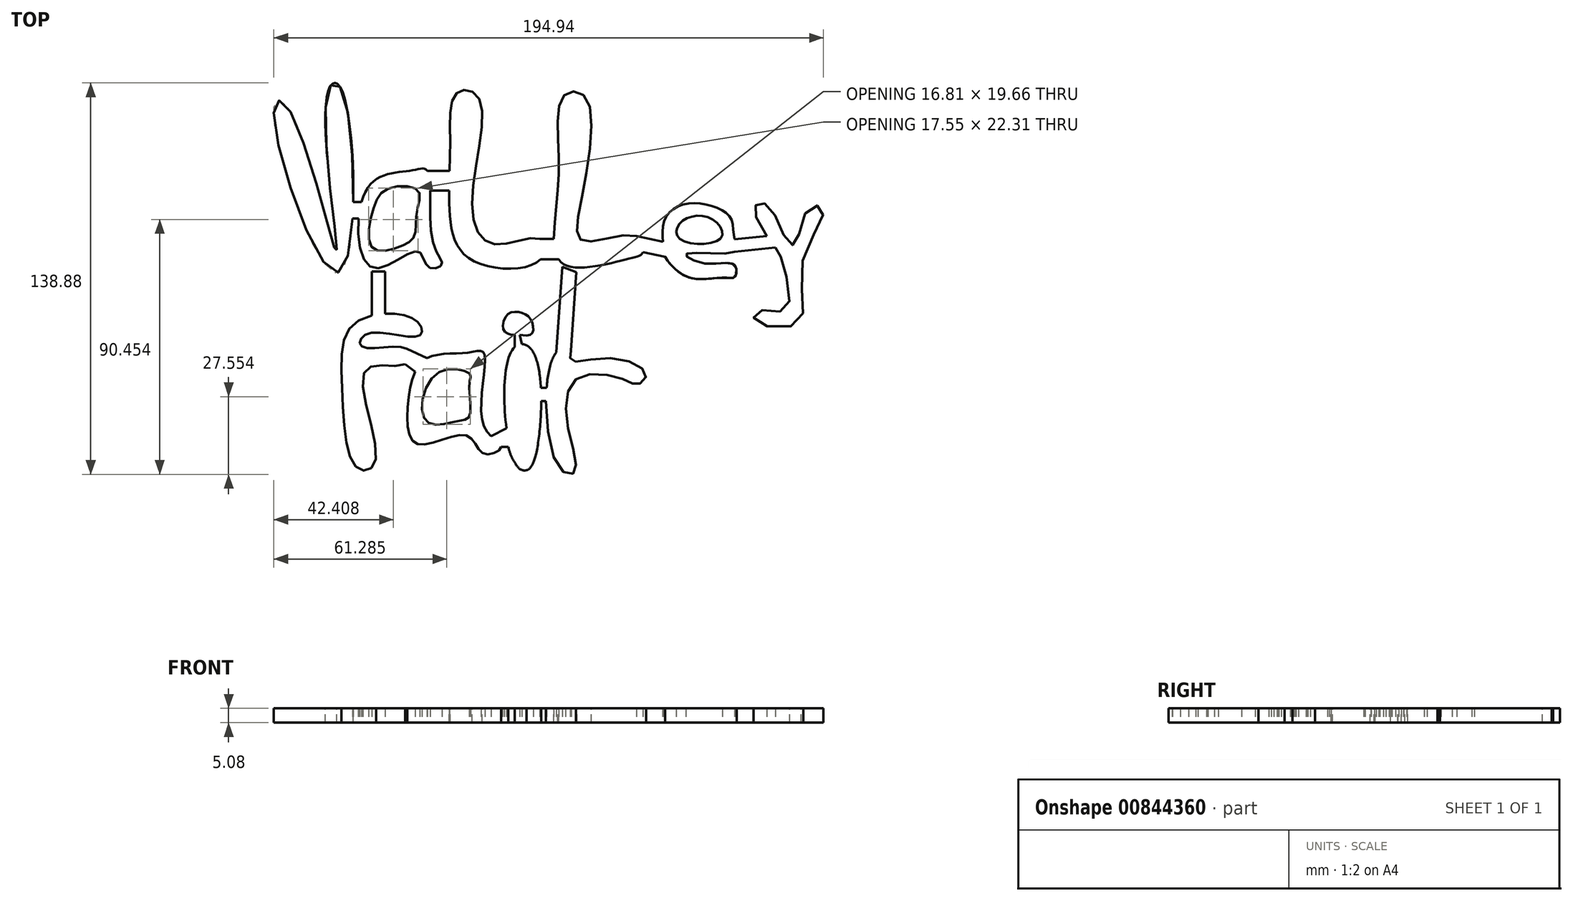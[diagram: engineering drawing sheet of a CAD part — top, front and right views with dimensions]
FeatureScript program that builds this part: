
annotation { "Feature Type Name" : "Feature", "Feature Type Description" : "" }
export const myFeature = defineFeature(function(context is Context, id is Id, definition is map)
    precondition{}
    {
        {
            var Q0;
            Q0=qCreatedBy(makeId("Top.planeOp"),FACE);
            var sketch = newSketch(context, id + "F0", { "sketchPlane" : qUnion([Q0])});
            skFitSpline(sketch, "E0", {"points": [v(-51.1, 46.73) * mm, v(-51.9, -19.2) * mm, v(-74.42, 39.6) * mm, v(-70.21, 40.25) * mm, v(-52.4, -11.9) * mm, v(-55.47, 44.78) * mm, v(-51.1, 46.73) * mm]});
            skFitSpline(sketch, "E1", {"points": [v(-25.67, 17.09) * mm, v(-41.38, 10.77) * mm, v(-39.6, -17.41) * mm, v(-23.57, -11.58) * mm, v(-19.84, -17.09) * mm, v(-15.14, -16.44) * mm, v(-18.06, -8.67) * mm, v(-20.16, 16.93) * mm, v(-25.67, 17.09) * mm]});
            skFitSpline(sketch, "E2", {"points": [v(-34.1, 10.6) * mm, v(-39.6, 2.51) * mm, v(-39.6, -10.45) * mm, v(-29.88, -9.96) * mm, v(-24.7, -6.07) * mm, v(-23.89, 2.19) * mm, v(-23.4, 9.96) * mm, v(-34.1, 10.6) * mm]});
            skFitSpline(sketch, "E3", {"points": [v(20, -14.5) * mm, v(-4.45, -14.66) * mm, v(-12.23, 2.19) * mm, v(-12.07, 26.8) * mm, v(-9.47, 44.78) * mm, v(-1.86, 42.68) * mm, v(-4.3, 5.1) * mm, v(3.8, -9.15) * mm, v(19.68, -7.2) * mm, v(20, -14.5) * mm]});
            skFitSpline(sketch, "E4", {"points": [v(52.07, -14) * mm, v(28.42, -16.28) * mm, v(25.19, 0) * mm, v(26.48, 23.4) * mm, v(28.42, 43.81) * mm, v(36.2, 42.68) * mm, v(33.93, 3.8) * mm, v(35.39, -8.02) * mm, v(54.01, -6.24) * mm, v(56.28, -11.9) * mm, v(52.07, -14) * mm]});
            skFitSpline(sketch, "E5", {"points": [v(69.4, -7.2) * mm, v(83.98, -6.88) * mm, v(80.58, 0) * mm, v(69.89, -1.21) * mm, v(69.4, -7.2) * mm]});
            skPoint(sketch, "E6.2.internal.orphan", {"position": v(87.54, 0) * mm});
            skFitSpline(sketch, "E7", {"points": [v(88.84, -7.37) * mm, v(87.54, 0) * mm, v(81.22, 4.3) * mm, v(70.86, 5.1) * mm, v(64.22, 0) * mm, v(63.4, -8.18) * mm, v(64.22, -13.52) * mm, v(70.37, -19.84) * mm, v(77.34, -21.46) * mm, v(86.08, -20.97) * mm, v(89, -20.65) * mm, v(88.84, -16.44) * mm, v(78.63, -15.95) * mm, v(71.67, -12.55) * mm, v(88.84, -11.74) * mm, v(88.84, -7.37) * mm]});
            skFitSpline(sketch, "E8", {"points": [v(103.26, -10.22) * mm, v(95.78, 2.45) * mm, v(97.22, 5.32) * mm, v(101.25, 4.17) * mm, v(107.87, -8.5) * mm, v(110.46, -8.78) * mm, v(115.35, 3.89) * mm, v(120.24, 3.02) * mm, v(112.76, -15.69) * mm, v(111.32, -36.98) * mm, v(96.07, -36.12) * mm, v(97.5, -32.67) * mm, v(107.3, -32.1) * mm, v(105.57, -14.53) * mm, v(103.26, -10.22) * mm]});
            skLineSegment(sketch, "E9", {"start": v(-46.4, 5.91) * mm, "end": v(-43.47, 5.91) * mm});
            skLineSegment(sketch, "E10", {"start": v(-46.64, 0) * mm, "end": v(-44.54, 0) * mm});
            skLineSegment(sketch, "E11", {"start": v(-20.16, 16.93) * mm, "end": v(-12.23, 16.93) * mm});
            skLineSegment(sketch, "E12", {"start": v(-12.23, 9.96) * mm, "end": v(-19.15, 9.96) * mm});
            skLineSegment(sketch, "E13", {"start": v(19.68, -7.2) * mm, "end": v(24.75, -7.2) * mm});
            skLineSegment(sketch, "E14", {"start": v(20, -14.5) * mm, "end": v(26.46, -14.5) * mm});
            skLineSegment(sketch, "E15", {"start": v(88.84, -11.74) * mm, "end": v(103.26, -10.22) * mm});
            skLineSegment(sketch, "E16", {"start": v(88.84, -7.37) * mm, "end": v(100.32, -6.16) * mm});
            skPoint(sketch, "E17.end.orphan", {"position": v(63.4, -11.9) * mm});
            skLineSegment(sketch, "E18", {"start": v(56.28, -11.9) * mm, "end": v(64.22, -13.52) * mm});
            skLineSegment(sketch, "E19", {"start": v(54.01, -6.24) * mm, "end": v(63.4, -8.18) * mm});
            skSolve(sketch);
        }
        {
            var Q0;
            Q0 = qSketchRegion(id + "F0", true);
            extrude(context, id + "F1", {"entities" : qUnion([Q0]), "depth" : 5.08 * mm, "offsetDistance" : 25.4 * mm});
        }
        {
            var Q0;
            Q0=qCreatedBy(makeId("Top.planeOp"),FACE);
            var sketch = newSketch(context, id + "F2", { "sketchPlane" : qUnion([Q0])});
            skFitSpline(sketch, "E20", {"points": [v(-5.2, -47.47) * mm, v(-20.26, -49.52) * mm, v(-26.76, -63.56) * mm, v(-23.68, -79.98) * mm, v(-6.23, -76.9) * mm, v(0, -83.4) * mm, v(6.1, -81.01) * mm, v(0, -73.82) * mm, v(0, -47.81) * mm, v(-5.2, -47.47) * mm]});
            skPoint(sketch, "E21.3.internal.orphan", {"position": v(-5.2, -70.06) * mm});
            skPoint(sketch, "E21.4.internal.orphan", {"position": v(-5.2, -55) * mm});
            skFitSpline(sketch, "E22", {"points": [v(-5.2, -55) * mm, v(-16.84, -55) * mm, v(-20.6, -71.77) * mm, v(-9.3, -71.77) * mm, v(-5.2, -70.06) * mm, v(-5.2, -58.42) * mm, v(-5.2, -55) * mm]});
            skFitSpline(sketch, "E23", {"points": [v(9.86, -46.79) * mm, v(10.88, -86.49) * mm, v(15, -89.23) * mm, v(18.41, -83.4) * mm, v(17.05, -46.79) * mm, v(9.86, -46.79) * mm]});
            skFitSpline(sketch, "E24", {"points": [v(33.47, -56.37) * mm, v(49.56, -57.05) * mm, v(54.7, -58.76) * mm, v(57.43, -55.34) * mm, v(45.11, -49.52) * mm, v(30.74, -50.2) * mm, v(30.74, -46.79) * mm, v(25.6, -47.47) * mm, v(26.29, -87.86) * mm, v(32.1, -89.91) * mm, v(29.37, -72.11) * mm, v(33.47, -56.37) * mm]});
            skPoint(sketch, "E25.6.internal.orphan", {"position": v(-27.45, -36.86) * mm});
            skPoint(sketch, "E25.7.internal.orphan", {"position": v(-27.45, -31.73) * mm});
            skFitSpline(sketch, "E26", {"points": [v(-38.64, -86.28) * mm, v(-42.16, -53.82) * mm, v(-27.98, -51.59) * mm, v(-27.35, -46.23) * mm, v(-43.43, -45.3) * mm, v(-41.55, -40.9) * mm, v(-22.95, -41.5) * mm, v(-24.22, -36.13) * mm, v(-45.66, -36.86) * mm, v(-50.34, -60.45) * mm, v(-44.94, -88.5) * mm, v(-38.64, -86.28) * mm]});
            skLineSegment(sketch, "E27", {"start": v(-27.98, -51.59) * mm, "end": v(-24.44, -54.28) * mm});
            skLineSegment(sketch, "E28", {"start": v(-27.35, -46.23) * mm, "end": v(-20.26, -49.52) * mm});
            skLineSegment(sketch, "E29", {"start": v(6.1, -81.01) * mm, "end": v(9.08, -81.01) * mm});
            skLineSegment(sketch, "E30", {"start": v(9.08, -81.01) * mm, "end": v(2.49, -77.23) * mm});
            skLineSegment(sketch, "E31", {"start": v(2.49, -77.23) * mm, "end": v(9.08, -73.82) * mm});
            skLineSegment(sketch, "E32", {"start": v(16.6, -46.21) * mm, "end": v(17.05, -46.79) * mm});
            skLineSegment(sketch, "E33", {"start": v(20.12, -59.97) * mm, "end": v(22.16, -59.97) * mm});
            skLineSegment(sketch, "E34", {"start": v(20.24, -64.76) * mm, "end": v(22.16, -64.76) * mm});
            skFitSpline(sketch, "E35", {"points": [v(10.88, -86.49) * mm, v(7.92, -74.43) * mm, v(9.86, -50.44) * mm, v(10.88, -46.79) * mm, v(13.95, -46.79) * mm, v(16.79, -51.07) * mm, v(20.12, -59.97) * mm, v(20.24, -64.76) * mm, v(18.41, -83.4) * mm, v(15, -89.23) * mm, v(10.88, -86.49) * mm]});
            skFitSpline(sketch, "E36", {"points": [v(10.79, -41.29) * mm, v(12.68, -41.29) * mm, v(16.79, -40.97) * mm, v(16.79, -36.24) * mm, v(13.31, -33.4) * mm, v(8.26, -34.03) * mm, v(7, -39.71) * mm, v(10.79, -41.29) * mm]});
            skLineSegment(sketch, "E37", {"start": v(12.68, -41.29) * mm, "end": v(13.95, -46.79) * mm});
            skLineSegment(sketch, "E38", {"start": v(10.79, -41.29) * mm, "end": v(10.88, -46.79) * mm});
            skPoint(sketch, "E39.end.orphan", {"position": v(-31.24, -14.88) * mm});
            skPoint(sketch, "E40.start.orphan", {"position": v(47.27, -14.88) * mm});
            skLineSegment(sketch, "E41", {"start": v(-39.8, -34.32) * mm, "end": v(-39.8, -18.81) * mm});
            skLineSegment(sketch, "E42", {"start": v(-35.14, -33.68) * mm, "end": v(-35.14, -18.81) * mm});
            skLineSegment(sketch, "E43", {"start": v(-39.8, -18.81) * mm, "end": v(-35.14, -18.81) * mm});
            skPoint(sketch, "E44.end.orphan", {"position": v(40.34, -49.52) * mm});
            skPoint(sketch, "E45.end.orphan", {"position": v(40.34, -18.64) * mm});
            skLineSegment(sketch, "E46", {"start": v(25.6, -47.47) * mm, "end": v(27.73, -17.04) * mm});
            skLineSegment(sketch, "E47", {"start": v(30.74, -46.79) * mm, "end": v(32.68, -18.97) * mm});
            skLineSegment(sketch, "E48", {"start": v(32.68, -18.97) * mm, "end": v(27.73, -17.04) * mm});
            skSolve(sketch);
        }
        {
            var Q0;
            Q0 = qSketchRegion(id + "F2", true);
            extrude(context, id + "F3", {"entities" : qUnion([Q0]), "depth" : 5.08 * mm, "offsetDistance" : 25.4 * mm});
        }
    });
